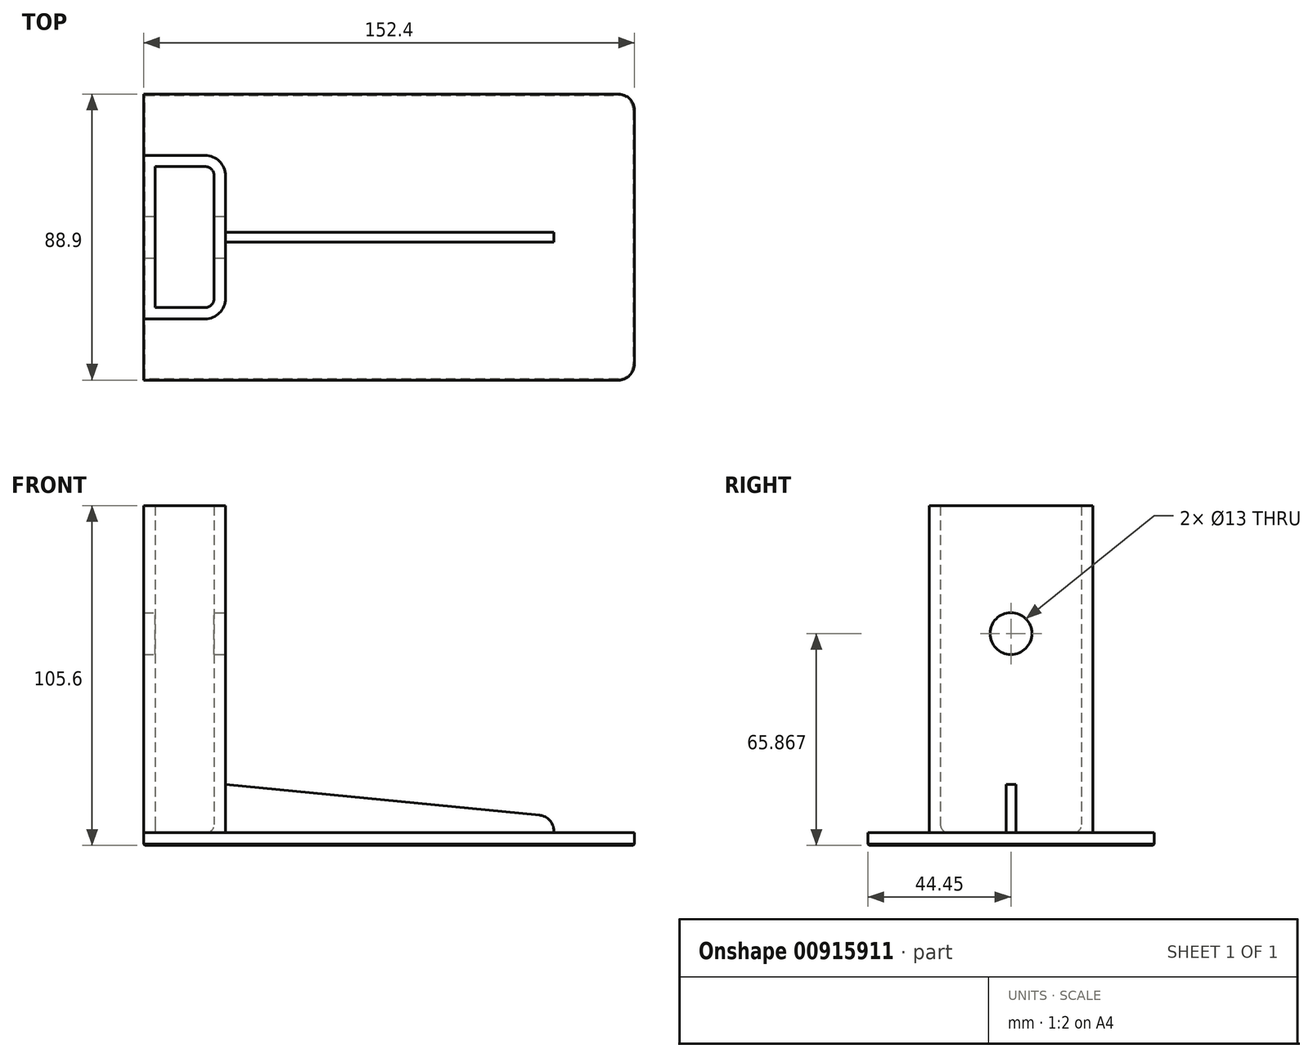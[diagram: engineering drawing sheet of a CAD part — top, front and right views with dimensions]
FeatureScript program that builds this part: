
annotation { "Feature Type Name" : "Feature", "Feature Type Description" : "" }
export const myFeature = defineFeature(function(context is Context, id is Id, definition is map)
    precondition{}
    {
        {
            var Q0;
            Q0=qCreatedBy(makeId("Top.planeOp"),FACE);
            var sketch = newSketch(context, id + "F0", { "sketchPlane" : qUnion([Q0])});
            skLineSegment(sketch, "E0.bottom", {"start": v(0, 44.45) * mm, "end": v(152.4, 44.45) * mm});
            skLineSegment(sketch, "E0.top", {"start": v(0, -44.45) * mm, "end": v(152.4, -44.45) * mm});
            skLineSegment(sketch, "E0.left", {"start": v(0, 44.45) * mm, "end": v(0, -44.45) * mm});
            skLineSegment(sketch, "E0.right", {"start": v(152.4, 44.45) * mm, "end": v(152.4, -44.45) * mm});
            skPoint(sketch, "E1", {"position": v(0, 0) * mm});
            skSolve(sketch);
        }
        {
            var Q0;
            Q0 = qSketchRegion(id + "F0", true);
            extrude(context, id + "F1", {"entities" : qUnion([Q0]), "depth" : 4 * mm, "offsetDistance" : 25 * mm});
        }
        {
            var Q0;
            Q0=makeQuery(id+"F1.opExtrude","SWEPT_EDGE",EDGE,{"disambiguationData":[OSD([sQuery(id+"F0.wireOp",EDGE,"E0.top"),sQuery(id+"F0.wireOp",EDGE,"E0.right")])]});
            var Q1;
            Q1=makeQuery(id+"F1.opExtrude","SWEPT_EDGE",EDGE,{"disambiguationData":[OSD([sQuery(id+"F0.wireOp",EDGE,"E0.bottom"),sQuery(id+"F0.wireOp",EDGE,"E0.right")])]});
            fillet(context, id + "F2", {"entities" : qUnion([Q0, Q1]), "radius" : 5 * mm, "tangentPropagation" : true, "allowEdgeOverflow" : false});
        }
        {
            var Q0;
            Q0=makeQuery(id+"F1.opExtrude","CAP_FACE",FACE,{"disambiguationData":[OSD([sQuery(id+"F0.wireOp",EDGE,"E0.bottom"),sQuery(id+"F0.wireOp",EDGE,"E0.top"),sQuery(id+"F0.wireOp",EDGE,"E0.left"),sQuery(id+"F0.wireOp",EDGE,"E0.right")])],"isStart":false});
            var sketch = newSketch(context, id + "F3", { "sketchPlane" : qUnion([Q0])});
            skLineSegment(sketch, "E2.0", {"start": v(0, 44.45) * mm, "end": v(0, -44.45) * mm});
            skPoint(sketch, "E3", {"position": v(0, 0) * mm});
            skLineSegment(sketch, "E4.bottom", {"start": v(0, 25.4) * mm, "end": v(25.4, 25.4) * mm});
            skLineSegment(sketch, "E4.top", {"start": v(0, -25.4) * mm, "end": v(25.4, -25.4) * mm});
            skLineSegment(sketch, "E4.left", {"start": v(0, 25.4) * mm, "end": v(0, -25.4) * mm});
            skLineSegment(sketch, "E4.right", {"start": v(25.4, 25.4) * mm, "end": v(25.4, -25.4) * mm});
            skSolve(sketch);
        }
        {
            var Q0;
            Q0=makeQuery(id+"F3.imprint","IMPRINT",FACE,{"disambiguationData":[TD([[makeQuery(id+"F3.imprint","IMPRINT",EDGE,{"derivedFrom":sQuery(id+"F3.wireOp",EDGE,"E4.bottom")}),-1.0]])]});
            extrude(context, id + "F4", {"entities" : qUnion([Q0]), "depth" : 101.6 * mm, "offsetDistance" : 25 * mm});
        }
        {
            var Q0;
            Q0=makeQuery(id+"F4.opExtrude","SWEPT_EDGE",EDGE,{"disambiguationData":[OSD([sQuery(id+"F3.wireOp",EDGE,"E4.top"),sQuery(id+"F3.wireOp",EDGE,"E4.right")])]});
            var Q1;
            Q1=makeQuery(id+"F4.opExtrude","SWEPT_EDGE",EDGE,{"disambiguationData":[OSD([sQuery(id+"F3.wireOp",EDGE,"E4.bottom"),sQuery(id+"F3.wireOp",EDGE,"E4.right")])]});
            fillet(context, id + "F5", {"entities" : qUnion([Q0, Q1]), "radius" : 6.35 * mm, "tangentPropagation" : true, "allowEdgeOverflow" : false});
        }
        {
            var Q0;
            Q0=makeQuery(id+"F4.opExtrude","CAP_FACE",FACE,{"disambiguationData":[OSD([sQuery(id+"F3.wireOp",EDGE,"E4.bottom"),sQuery(id+"F3.wireOp",EDGE,"E4.top"),sQuery(id+"F3.wireOp",EDGE,"E4.left"),sQuery(id+"F3.wireOp",EDGE,"E4.right")])],"isStart":false});
            var Q1;
            Q1=makeQuery(id+"F4.opExtrude","SWEPT_FACE",FACE,{"disambiguationData":[OSD([sQuery(id+"F3.wireOp",EDGE,"E4.left")])]});
            var Q2;
            Q2=makeQuery(id+"F4.opExtrude","CAP_FACE",FACE,{"disambiguationData":[OSD([sQuery(id+"F3.wireOp",EDGE,"E4.bottom"),sQuery(id+"F3.wireOp",EDGE,"E4.top"),sQuery(id+"F3.wireOp",EDGE,"E4.left"),sQuery(id+"F3.wireOp",EDGE,"E4.right")])],"isStart":true});
            shell(context, id + "F6", {"entities" : qUnion([Q0, Q1, Q2]), "thickness" : 3.5 * mm});
        }
        {
            var Q0;
            Q0=makeQuery(id+"F1.opExtrude","SWEPT_BODY",BODY,{"disambiguationData":[OSD([sQuery(id+"F0.wireOp",EDGE,"E0.bottom"),sQuery(id+"F0.wireOp",EDGE,"E0.top"),sQuery(id+"F0.wireOp",EDGE,"E0.left"),sQuery(id+"F0.wireOp",EDGE,"E0.right")])]});
            var Q1;
            Q1=makeQuery(id+"F4.opExtrude","SWEPT_BODY",BODY,{"disambiguationData":[OSD([sQuery(id+"F3.wireOp",EDGE,"E4.bottom"),sQuery(id+"F3.wireOp",EDGE,"E4.top"),sQuery(id+"F3.wireOp",EDGE,"E4.left"),sQuery(id+"F3.wireOp",EDGE,"E4.right")])]});
            booleanBodies(context, id + "F7", {"operationType" : BooleanOperationType.UNION, "tools" : qUnion([Q0, Q1])});
        }
        {
            var Q0;
            Q0=qCreatedBy(makeId("Front.planeOp"),FACE);
            var sketch = newSketch(context, id + "F8", { "sketchPlane" : qUnion([Q0])});
            skLineSegment(sketch, "E5.0.1", {"start": v(25.4, 105.6) * mm, "end": v(25.4, 4) * mm});
            skLineSegment(sketch, "E5.0.3", {"start": v(25.4, 4) * mm, "end": v(25.4, 105.6) * mm});
            skLineSegment(sketch, "E6.0.1", {"start": v(0, 4) * mm, "end": v(19.05, 4) * mm});
            skLineSegment(sketch, "E6.0.2", {"start": v(19.05, 4) * mm, "end": v(25.4, 4) * mm});
            skLineSegment(sketch, "E6.0.4", {"start": v(25.4, 4) * mm, "end": v(19.05, 4) * mm});
            skLineSegment(sketch, "E6.0.5", {"start": v(19.05, 4) * mm, "end": v(0, 4) * mm});
            skLineSegment(sketch, "E6.0.7", {"start": v(0, 4) * mm, "end": v(147.4, 4) * mm});
            skLineSegment(sketch, "E6.0.8", {"start": v(147.4, 4) * mm, "end": v(152.4, 4) * mm});
            skLineSegment(sketch, "E6.0.10", {"start": v(152.4, 4) * mm, "end": v(147.4, 4) * mm});
            skLineSegment(sketch, "E6.0.11", {"start": v(147.4, 4) * mm, "end": v(0, 4) * mm});
            skLineSegment(sketch, "E7", {"start": v(25.4, 19) * mm, "end": v(127.4, 9) * mm});
            skLineSegment(sketch, "E8", {"start": v(127.4, 9) * mm, "end": v(127.4, 4) * mm});
            skSolve(sketch);
        }
        {
            var Q0;
            {var subQ3=sQuery(id+"F8.wireOp",EDGE,"E7");Q0=makeQuery(id+"F8.imprint","IMPRINT",FACE,{"disambiguationData":[TD([[makeQuery(id+"F8.imprint","IMPRINT",EDGE,{"derivedFrom":subQ3}),-1.0]])]});}
            extrude(context, id + "F9", {"entities" : qUnion([Q0]), "operationType" : NewBodyOperationType.ADD, "endBound" : BoundingType.SYMMETRIC, "depth" : 3 * mm, "offsetDistance" : 25 * mm});
        }
        {
            var Q0;
            Q0=makeQuery(id+"F9.opExtrude","SWEPT_EDGE",EDGE,{"disambiguationData":[OSD([sQuery(id+"F8.wireOp",EDGE,"E7"),sQuery(id+"F8.wireOp",EDGE,"E8")])]});
            fillet(context, id + "F10", {"entities" : qUnion([Q0]), "radius" : 5 * mm, "tangentPropagation" : true, "allowEdgeOverflow" : false});
        }
        {
            var Q0;
            Q0=makeQuery(id+"F4.opExtrude","CAP_EDGE",EDGE,{"disambiguationData":[OSD([sQuery(id+"F3.wireOp",EDGE,"E4.top")])],"isStart":true});
            var Q1;
            {var subQ0=sQuery(id+"F3.wireOp",EDGE,"E4.bottom");Q1=makeQuery(id+"F6.opShell","OFFSET_EDGE",EDGE,{"disambiguationData":[OSD([subQ0]),TDD([makeQuery(id+"F4.opExtrude","CAP_EDGE",EDGE,{"disambiguationData":[OSD([subQ0])],"isStart":true})])]});}
            var Q2;
            {var subQ0=sQuery(id+"F3.wireOp",EDGE,"E4.right");Q2=makeQuery(id+"F9.boolean.opBoolean","SPLIT",EDGE,{"disambiguationData":[TD([makeQuery(id+"F5.opFillet","BLEND_FACE",FACE,{"disambiguationData":[OSD([sQuery(id+"F3.wireOp",EDGE,"E4.bottom"),subQ0])]})])],"derivedFrom":makeQuery(id+"F4.opExtrude","CAP_EDGE",EDGE,{"disambiguationData":[OSD([subQ0])],"isStart":true})});}
            var Q3;
            Q3=makeQuery(id+"F9.opExtrude","CAP_EDGE",EDGE,{"disambiguationData":[OSD([sQuery(id+"F8.wireOp",EDGE,"E6.0.11")])],"isStart":true});
            var Q4;
            Q4=makeQuery(id+"F9.opExtrude","CAP_EDGE",EDGE,{"disambiguationData":[OSD([sQuery(id+"F8.wireOp",EDGE,"E6.0.11")])],"isStart":false});
            var Q5;
            Q5=makeQuery(id+"F9.opExtrude","SWEPT_EDGE",EDGE,{"disambiguationData":[OSD([sQuery(id+"F8.wireOp",EDGE,"E6.0.11"),sQuery(id+"F8.wireOp",EDGE,"E8")])]});
            var Q6;
            Q6=makeQuery(id+"F9.opExtrude","SWEPT_EDGE",EDGE,{"disambiguationData":[OSD([sQuery(id+"F8.wireOp",EDGE,"E5.0.3"),sQuery(id+"F8.wireOp",EDGE,"E7")])]});
            var Q7;
            Q7=makeQuery(id+"F9.opExtrude","CAP_EDGE",EDGE,{"disambiguationData":[OSD([sQuery(id+"F8.wireOp",EDGE,"E5.0.3")])],"isStart":false});
            var Q8;
            Q8=makeQuery(id+"F9.opExtrude","CAP_EDGE",EDGE,{"disambiguationData":[OSD([sQuery(id+"F8.wireOp",EDGE,"E5.0.3")])],"isStart":true});
            fillet(context, id + "F11", {"entities" : qUnion([Q0, Q1, Q2, Q3, Q4, Q5, Q6, Q7, Q8]), "radius" : 2.5 * mm, "tangentPropagation" : true, "allowEdgeOverflow" : false});
        }
        {
            var Q0;
            Q0=makeQuery(id+"F4.opExtrude","SWEPT_FACE",FACE,{"disambiguationData":[OSD([sQuery(id+"F3.wireOp",EDGE,"E4.right")])]});
            var sketch = newSketch(context, id + "F12", { "sketchPlane" : qUnion([Q0])});
            skCircle(sketch, "E9", {"center": v(0, 65.87) * mm, "radius": 6.5 * mm});
            skSolve(sketch);
        }
        {
            var Q0;
            Q0 = qSketchRegion(id + "F12", true);
            extrude(context, id + "F13", {"entities" : qUnion([Q0]), "operationType" : NewBodyOperationType.REMOVE, "endBound" : BoundingType.THROUGH_ALL, "oppositeDirection" : true, "depth" : 25 * mm, "offsetDistance" : 25 * mm});
        }
        {
            var Q0;
            Q0=makeQuery(id+"F1.opExtrude","CAP_FACE",FACE,{"disambiguationData":[OSD([sQuery(id+"F0.wireOp",EDGE,"E0.bottom"),sQuery(id+"F0.wireOp",EDGE,"E0.top"),sQuery(id+"F0.wireOp",EDGE,"E0.left"),sQuery(id+"F0.wireOp",EDGE,"E0.right")])],"isStart":true});
            chamfer(context, id + "F14", {"entities" : qUnion([Q0]), "width" : .375 * mm, "tangentPropagation" : true});
        }
    });
